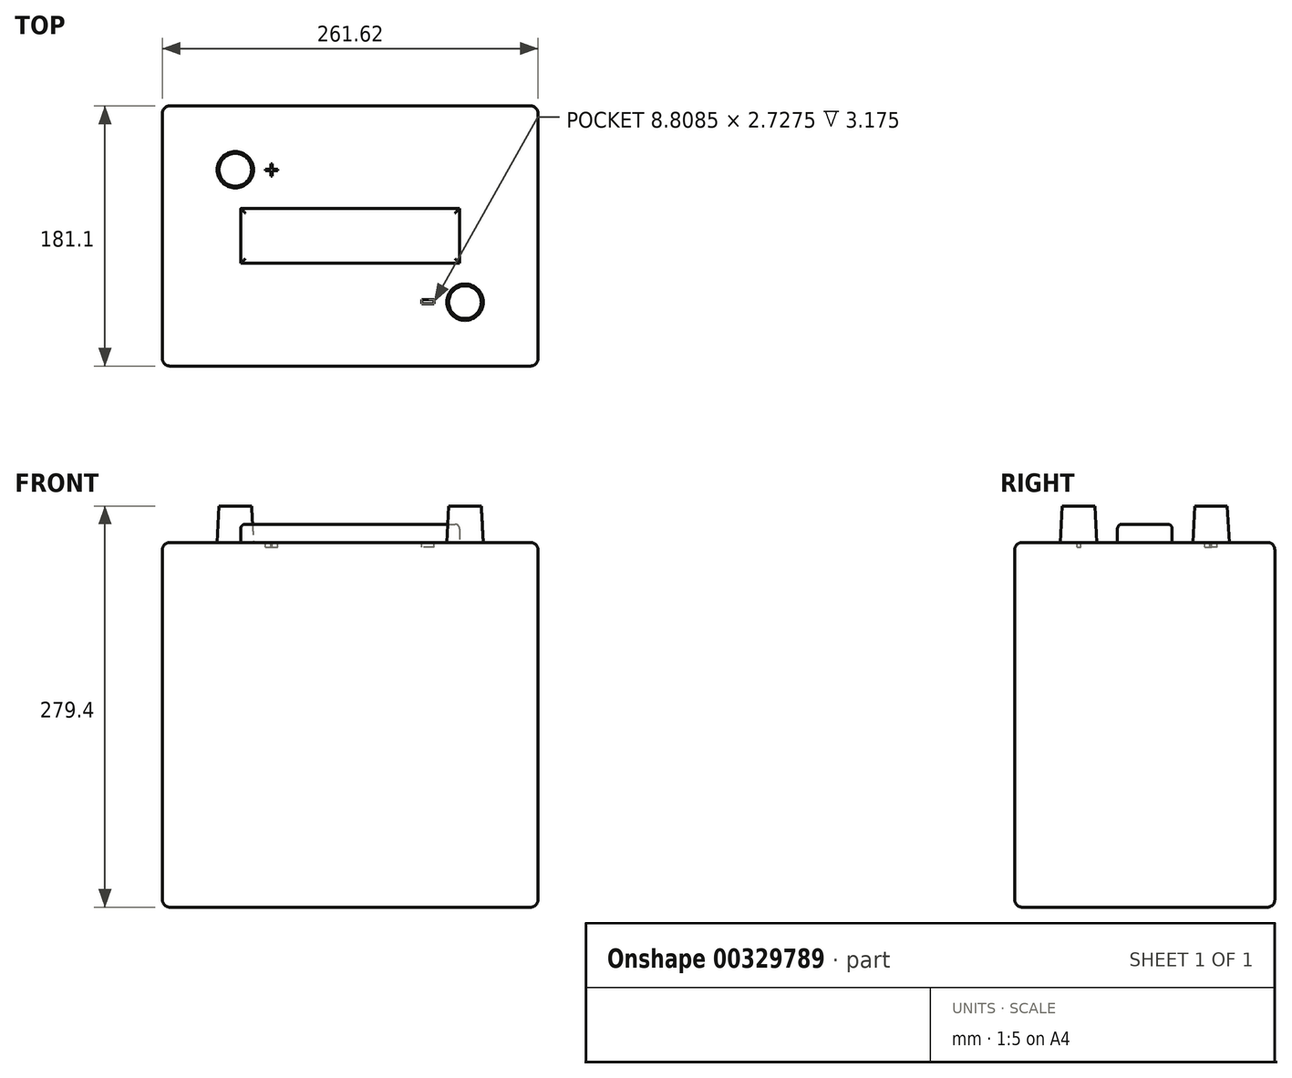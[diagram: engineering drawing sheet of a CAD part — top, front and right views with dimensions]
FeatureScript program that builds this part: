
annotation { "Feature Type Name" : "Feature", "Feature Type Description" : "" }
export const myFeature = defineFeature(function(context is Context, id is Id, definition is map)
    precondition{}
    {
        {
            var Q0;
            Q0=qCreatedBy(makeId("Front.planeOp"),FACE);
            var sketch = newSketch(context, id + "F0", { "sketchPlane" : qUnion([Q0])});
            skLineSegment(sketch, "E0.bottom", {"start": v(0, 0) * mm, "end": v(-261.62, 0) * mm});
            skLineSegment(sketch, "E0.top", {"start": v(0, 254) * mm, "end": v(-261.62, 254) * mm});
            skLineSegment(sketch, "E0.left", {"start": v(0, 0) * mm, "end": v(0, 254) * mm});
            skLineSegment(sketch, "E0.right", {"start": v(-261.62, 0) * mm, "end": v(-261.62, 254) * mm});
            skSolve(sketch);
        }
        {
            var Q0;
            Q0 = qSketchRegion(id + "F0", true);
            extrude(context, id + "F1", {"entities" : qUnion([Q0]), "depth" : 181.1 * mm});
        }
        {
            var Q0;
            Q0=makeQuery(id+"F1.opExtrude","CAP_FACE",FACE,{"disambiguationData":[OSD([sQuery(id+"F0.wireOp",EDGE,"E0.bottom"),sQuery(id+"F0.wireOp",EDGE,"E0.top"),sQuery(id+"F0.wireOp",EDGE,"E0.left"),sQuery(id+"F0.wireOp",EDGE,"E0.right")])],"isStart":false});
            var Q1;
            Q1=makeQuery(id+"F1.opExtrude","SWEPT_FACE",FACE,{"disambiguationData":[OSD([sQuery(id+"F0.wireOp",EDGE,"E0.top")])]});
            var Q2;
            Q2=makeQuery(id+"F1.opExtrude","CAP_FACE",FACE,{"disambiguationData":[OSD([sQuery(id+"F0.wireOp",EDGE,"E0.bottom"),sQuery(id+"F0.wireOp",EDGE,"E0.top"),sQuery(id+"F0.wireOp",EDGE,"E0.left"),sQuery(id+"F0.wireOp",EDGE,"E0.right")])],"isStart":true});
            var Q3;
            Q3=makeQuery(id+"F1.opExtrude","SWEPT_FACE",FACE,{"disambiguationData":[OSD([sQuery(id+"F0.wireOp",EDGE,"E0.bottom")])]});
            fillet(context, id + "F2", {"entities" : qUnion([Q0, Q1, Q2, Q3]), "radius" : 5.08 * mm, "tangentPropagation" : true, "allowEdgeOverflow" : false});
        }
        {
            var Q0;
            Q0=makeQuery(id+"F1.opExtrude","SWEPT_FACE",FACE,{"disambiguationData":[OSD([sQuery(id+"F0.wireOp",EDGE,"E0.top")])]});
            var sketch = newSketch(context, id + "F3", { "sketchPlane" : qUnion([Q0])});
            skCircle(sketch, "E1", {"center": v(-210.82, -44.45) * mm, "radius": 12.7 * mm});
            skCircle(sketch, "E2", {"center": v(-50.8, -136.65) * mm, "radius": 12.7 * mm});
            skLineSegment(sketch, "E3.bottom", {"start": v(-207.01, -109.6) * mm, "end": v(-54.61, -109.6) * mm});
            skLineSegment(sketch, "E3.top", {"start": v(-207.01, -71.5) * mm, "end": v(-54.61, -71.5) * mm});
            skLineSegment(sketch, "E3.left", {"start": v(-207.01, -109.6) * mm, "end": v(-207.01, -71.5) * mm});
            skLineSegment(sketch, "E3.right", {"start": v(-54.61, -109.6) * mm, "end": v(-54.61, -71.5) * mm});
            skText(sketch, "E4", { "text": "+", "fontName": "OpenSans-Regular.ttf"});
            skText(sketch, "E5", { "text": "-", "fontName": "OpenSans-Regular.ttf"});
            const initialGuessF3  = {"E4": [-0.19058, -0.0508, 1, 0, 0.0127], "E5": [-0.08255, -0.14618, 1, 0, 0.02646]};
            skSetInitialGuess(sketch, initialGuessF3);
            skSolve(sketch);
        }
        {
            var Q0;
            Q0=makeQuery(id+"F3.imprint","IMPRINT",FACE,{"disambiguationData":[TD([[makeQuery(id+"F3.imprint","IMPRINT",EDGE,{"derivedFrom":sQuery(id+"F3.wireOp",EDGE,"E3.bottom")}),1.0]])]});
            extrude(context, id + "F4", {"entities" : qUnion([Q0]), "operationType" : NewBodyOperationType.ADD, "depth" : 12.7 * mm});
        }
        {
            var Q0;
            Q0=makeQuery(id+"F3.imprint","IMPRINT",FACE,{"disambiguationData":[TD([[makeQuery(id+"F3.imprint","IMPRINT",EDGE,{"derivedFrom":sQuery(id+"F3.wireOp",EDGE,"E1")}),1.0]])]});
            var Q1;
            Q1=makeQuery(id+"F3.imprint","IMPRINT",FACE,{"disambiguationData":[TD([[makeQuery(id+"F3.imprint","IMPRINT",EDGE,{"derivedFrom":sQuery(id+"F3.wireOp",EDGE,"E2")}),1.0]])]});
            extrude(context, id + "F5", {"entities" : qUnion([Q0, Q1]), "operationType" : NewBodyOperationType.ADD, "depth" : 25.4 * mm, "hasDraft" : true, "draftAngle" : 3 * degree, "draftPullDirection" : true});
        }
        {
            var Q0;
            Q0=makeQuery(id+"F4.opExtrude","CAP_FACE",FACE,{"disambiguationData":[OSD([sQuery(id+"F3.wireOp",EDGE,"E3.bottom"),sQuery(id+"F3.wireOp",EDGE,"E3.top"),sQuery(id+"F3.wireOp",EDGE,"E3.left"),sQuery(id+"F3.wireOp",EDGE,"E3.right")])],"isStart":false});
            fillet(context, id + "F6", {"entities" : qUnion([Q0]), "radius" : 3.17 * mm, "tangentPropagation" : true, "allowEdgeOverflow" : false});
        }
        {
            var Q0;
            Q0=makeQuery(id+"F3.imprint","IMPRINT",FACE,{"disambiguationData":[TD([[makeQuery(id+"F3.imprint","IMPRINT",EDGE,{"derivedFrom":sQuery(id+"F3.wireOp",EDGE,"E4.sketch_text.stroke-0")}),-1.0]])]});
            var Q1;
            Q1=makeQuery(id+"F3.imprint","IMPRINT",FACE,{"disambiguationData":[TD([[makeQuery(id+"F3.imprint","IMPRINT",EDGE,{"derivedFrom":sQuery(id+"F3.wireOp",EDGE,"E5.sketch_text.stroke-0")}),-1.0]])]});
            extrude(context, id + "F7", {"entities" : qUnion([Q0, Q1]), "operationType" : NewBodyOperationType.REMOVE, "oppositeDirection" : true, "depth" : 3.17 * mm});
        }
    });
